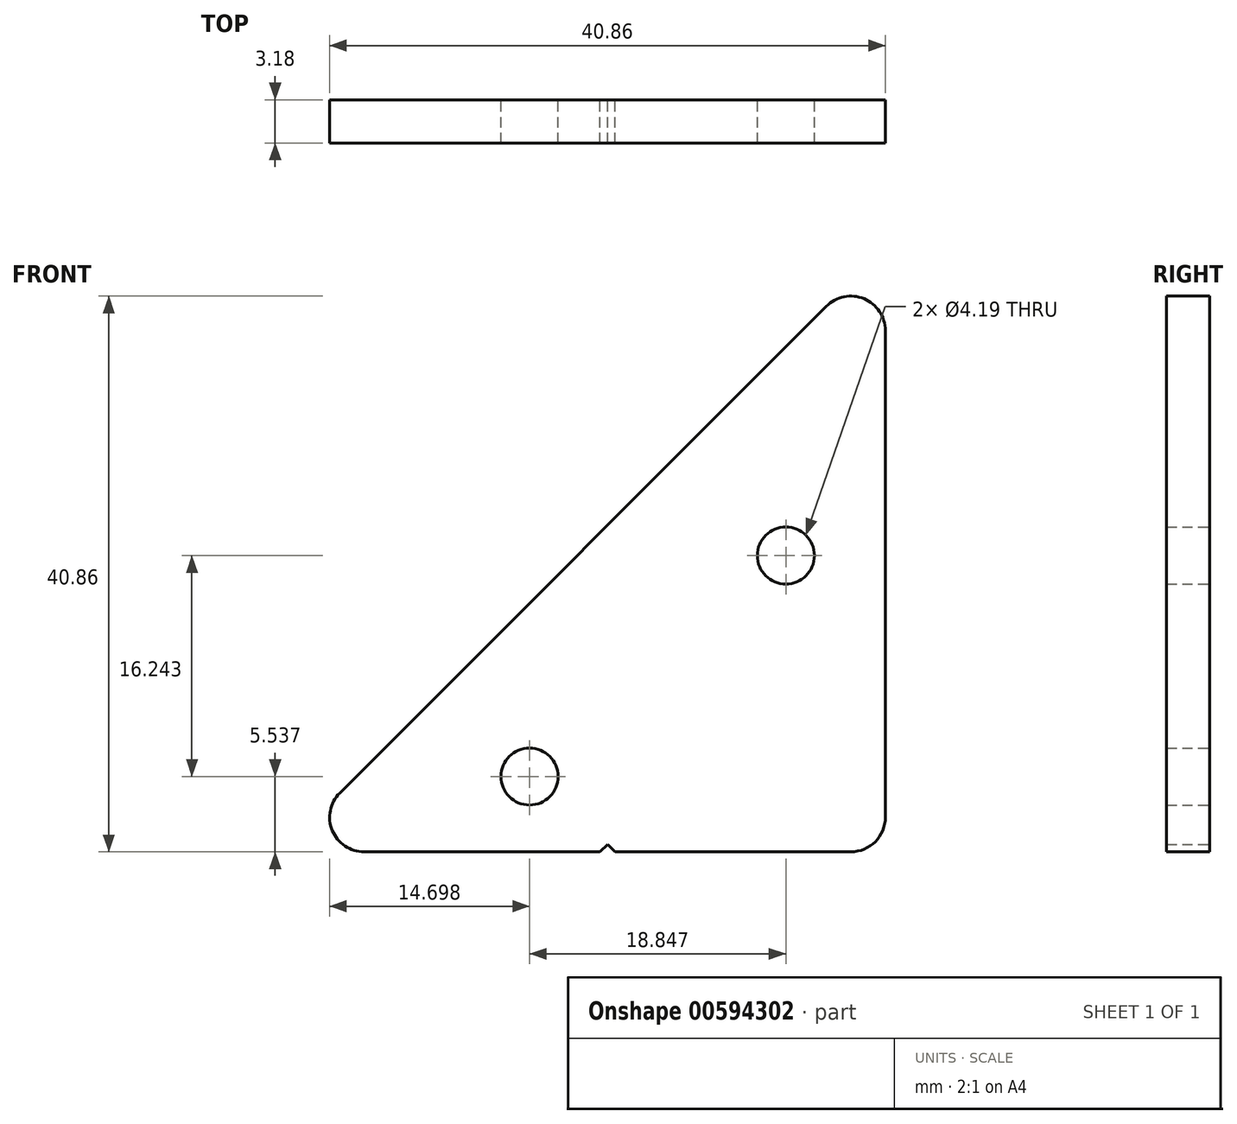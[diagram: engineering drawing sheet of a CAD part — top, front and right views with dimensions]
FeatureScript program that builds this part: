
annotation { "Feature Type Name" : "Feature", "Feature Type Description" : "" }
export const myFeature = defineFeature(function(context is Context, id is Id, definition is map)
    precondition{}
    {
        {
            var Q0;
            Q0=qCreatedBy(makeId("Front.planeOp"),FACE);
            var sketch = newSketch(context, id + "F0", { "sketchPlane" : qUnion([Q0])});
            skLineSegment(sketch, "E0", {"start": v(0, 2.54) * mm, "end": v(0, 38.32) * mm});
            skLineSegment(sketch, "E1", {"start": v(-4.34, 40.11) * mm, "end": v(-40.11, 4.34) * mm});
            skLineSegment(sketch, "E2", {"start": v(-38.32, 0) * mm, "end": v(-20.98, 0) * mm});
            skCircle(sketch, "E3", {"center": v(-7.32, 21.78) * mm, "radius": 2.1 * mm});
            skCircle(sketch, "E4", {"center": v(-26.16, 5.54) * mm, "radius": 2.1 * mm});
            skPoint(sketch, "E5.visualSharp", {"position": v(0, 44.45) * mm});
            skArc(sketch, "E5.filletArc", {"start": v(0, 38.32) * mm, "mid": v(-1.57, 40.66) * mm, "end": v(-4.34, 40.11) * mm});
            skPoint(sketch, "E6.visualSharp", {"position": v(-44.45, 0) * mm});
            skArc(sketch, "E6.filletArc", {"start": v(-40.11, 4.34) * mm, "mid": v(-40.66, 1.57) * mm, "end": v(-38.32, 0) * mm});
            skPoint(sketch, "E7.visualSharp", {"position": v(0, 0) * mm});
            skArc(sketch, "E7.filletArc", {"start": v(-2.54, 0) * mm, "mid": v(-0.74, 0.74) * mm, "end": v(0, 2.54) * mm});
            skPoint(sketch, "E8", {"position": v(-20.43, 0) * mm});
            skLineSegment(sketch, "E9", {"start": v(-20.43, 0.55) * mm, "end": v(-20.98, 0) * mm});
            skLineSegment(sketch, "E10", {"start": v(-20.43, 0.55) * mm, "end": v(-19.88, 0) * mm});
            skLineSegment(sketch, "E11.trimOffspring", {"start": v(-19.88, 0) * mm, "end": v(-2.54, 0) * mm});
            skSolve(sketch);
        }
        {
            var Q0;
            Q0 = qSketchRegion(id + "F0", true);
            extrude(context, id + "F1", {"entities" : qUnion([Q0]), "depth" : 3.17 * mm, "offsetDistance" : 25.4 * mm});
        }
    });
